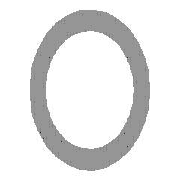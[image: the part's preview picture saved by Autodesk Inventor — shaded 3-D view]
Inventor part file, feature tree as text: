
AUTODESK INVENTOR PART (.ipt)
format: ipt  version: 2025 (Build 290162010, 162A)  size: 121,344 bytes
history: native  units: mm (DEFAULTED — no unit token found)
features: other x3, sketch x1, plane x1
ambient origin geometry x8: Origin, YZ Plane, XZ Plane, XY Plane, X Axis, Y Axis, Z Axis, Center Point
bodies: Solid1 (feature_tree), Body (feature_tree)
feature tree (5):
  other  "Driven Length"
  other  "Start plane"
  other  "End plane"
  sketch  "Sketch3"  dims[d0=88.9mm d1=2.0mm d2=300.0mm d3=0.0mm d4=-0.0mm d5=300.0mm d6=90.0deg d7=300.0mm]
  plane  "Work Plane3"
